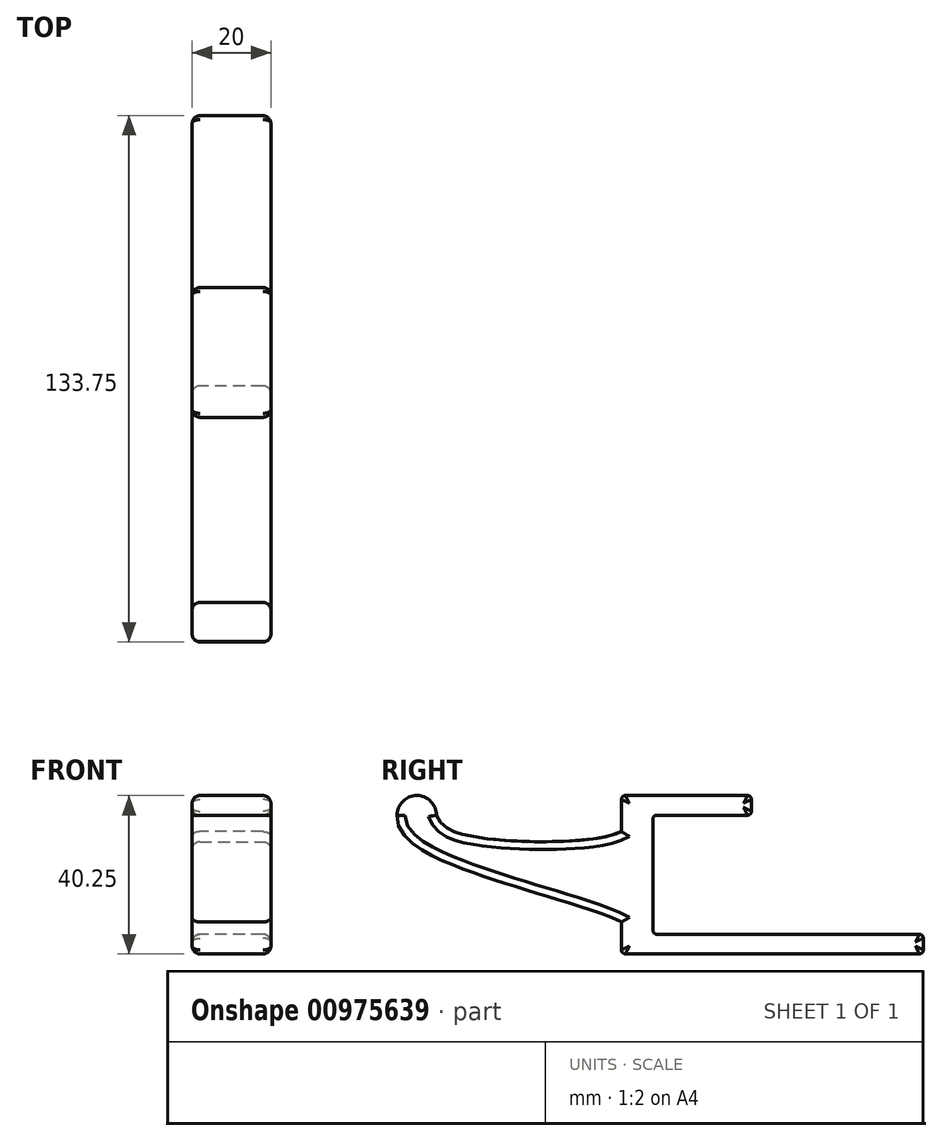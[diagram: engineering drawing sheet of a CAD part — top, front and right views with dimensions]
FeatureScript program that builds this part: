
annotation { "Feature Type Name" : "Feature", "Feature Type Description" : "" }
export const myFeature = defineFeature(function(context is Context, id is Id, definition is map)
    precondition{}
    {
        {
            var Q0;
            Q0=qCreatedBy(makeId("Right.planeOp"),FACE);
            var sketch = newSketch(context, id + "F0", { "sketchPlane" : qUnion([Q0])});
            skLineSegment(sketch, "E0", {"start": v(-1, 0) * mm, "end": v(-24, 0) * mm});
            skLineSegment(sketch, "E1", {"start": v(-25, -1) * mm, "end": v(-25, -29.25) * mm});
            skLineSegment(sketch, "E2", {"start": v(-24, -30.25) * mm, "end": v(42.67, -30.25) * mm});
            skLineSegment(sketch, "E3", {"start": v(43.67, -31.25) * mm, "end": v(43.67, -34.25) * mm});
            skLineSegment(sketch, "E4", {"start": v(42.67, -35.25) * mm, "end": v(-32, -35.25) * mm});
            skLineSegment(sketch, "E5", {"start": v(-33, -34.25) * mm, "end": v(-33, 4) * mm});
            skLineSegment(sketch, "E6", {"start": v(-32, 5) * mm, "end": v(-1, 5) * mm});
            skLineSegment(sketch, "E7", {"start": v(0, 4) * mm, "end": v(0, 1) * mm});
            skPoint(sketch, "E8.visualSharp", {"position": v(-33, 5) * mm});
            skArc(sketch, "E8.filletArc", {"start": v(-32, 5) * mm, "mid": v(-32.7, 4.7) * mm, "end": v(-33, 4) * mm});
            skPoint(sketch, "E9.visualSharp", {"position": v(0, 5) * mm});
            skArc(sketch, "E9.filletArc", {"start": v(0, 4) * mm, "mid": v(-0.3, 4.7) * mm, "end": v(-1, 5) * mm});
            skPoint(sketch, "E10.visualSharp", {"position": v(0, 0) * mm});
            skArc(sketch, "E10.filletArc", {"start": v(-1, 0) * mm, "mid": v(-0.3, 0.3) * mm, "end": v(0, 1) * mm});
            skPoint(sketch, "E11.visualSharp", {"position": v(-25, 0) * mm});
            skArc(sketch, "E11.filletArc", {"start": v(-24, 0) * mm, "mid": v(-24.7, -0.3) * mm, "end": v(-25, -1) * mm});
            skPoint(sketch, "E12.visualSharp", {"position": v(-25, -30.25) * mm});
            skArc(sketch, "E12.filletArc", {"start": v(-25, -29.25) * mm, "mid": v(-24.7, -29.96) * mm, "end": v(-24, -30.25) * mm});
            skPoint(sketch, "E13.visualSharp", {"position": v(-33, -35.25) * mm});
            skArc(sketch, "E13.filletArc", {"start": v(-33, -34.25) * mm, "mid": v(-32.7, -34.96) * mm, "end": v(-32, -35.25) * mm});
            skPoint(sketch, "E14.visualSharp", {"position": v(43.67, -35.25) * mm});
            skArc(sketch, "E14.filletArc", {"start": v(42.67, -35.25) * mm, "mid": v(43.37, -34.96) * mm, "end": v(43.67, -34.25) * mm});
            skPoint(sketch, "E15.visualSharp", {"position": v(43.67, -30.25) * mm});
            skArc(sketch, "E15.filletArc", {"start": v(43.67, -31.25) * mm, "mid": v(43.37, -30.54) * mm, "end": v(42.67, -30.25) * mm});
            skSolve(sketch);
        }
        {
            var Q0;
            Q0 = qSketchRegion(id + "F0", true);
            extrude(context, id + "F1", {"entities" : qUnion([Q0]), "endBound" : BoundingType.SYMMETRIC, "depth" : 20 * mm, "offsetDistance" : 25 * mm});
        }
        {
            var Q0;
            Q0=qCreatedBy(makeId("Right.planeOp"),FACE);
            var sketch = newSketch(context, id + "F2", { "sketchPlane" : qUnion([Q0])});
            skLineSegment(sketch, "E16.0.1", {"start": v(-28, 0) * mm, "end": v(-28, -32.2) * mm});
            skLineSegment(sketch, "E16.0.3", {"start": v(-28, -32.2) * mm, "end": v(-28, 0) * mm});
            skFitSpline(sketch, "E17", {"points": [v(-28, 0) * mm, v(-36.23, -5.25) * mm, v(-74.18, -4.6) * mm, v(-80, 0) * mm], "startDerivative": vector(-20.31, -26.28) * mm, "endDerivative": vector(-9.72, 25.78) * mm});
            skFitSpline(sketch, "E18", {"points": [v(-28, -32.2) * mm, v(-38.78, -24.79) * mm, v(-83.12, -9.19) * mm, v(-89.68, -2.75) * mm, v(-90, 0) * mm], "startDerivative": vector(-14.07, 42.47) * mm, "endDerivative": vector(5.3, 40.48) * mm});
            skArc(sketch, "E19", {"start": v(-80, 0) * mm, "mid": v(-85, 5) * mm, "end": v(-90, 0) * mm});
            skPoint(sketch, "E20.orphan", {"position": v(-28, 4) * mm});
            skPoint(sketch, "E21.orphan", {"position": v(-28, -34.5) * mm});
            skSolve(sketch);
        }
        {
            var Q0;
            Q0 = qSketchRegion(id + "F2", true);
            extrude(context, id + "F3", {"entities" : qUnion([Q0]), "operationType" : NewBodyOperationType.ADD, "endBound" : BoundingType.SYMMETRIC, "depth" : 20 * mm, "offsetDistance" : 25 * mm});
        }
        {
            var Q0;
            Q0=makeQuery(id+"F3.opExtrude","CAP_FACE",FACE,{"disambiguationData":[OSD([sQuery(id+"F2.wireOp",EDGE,"E16.0.3"),sQuery(id+"F2.wireOp",EDGE,"E17"),sQuery(id+"F2.wireOp",EDGE,"E18"),sQuery(id+"F2.wireOp",EDGE,"E19")])],"isStart":true});
            var Q1;
            Q1=makeQuery(id+"F3.opExtrude","CAP_FACE",FACE,{"disambiguationData":[OSD([sQuery(id+"F2.wireOp",EDGE,"E16.0.3"),sQuery(id+"F2.wireOp",EDGE,"E17"),sQuery(id+"F2.wireOp",EDGE,"E18"),sQuery(id+"F2.wireOp",EDGE,"E19")])],"isStart":false});
            fillet(context, id + "F4", {"entities" : qUnion([Q0, Q1]), "radius" : 2 * mm, "tangentPropagation" : true, "allowEdgeOverflow" : false});
        }
    });
